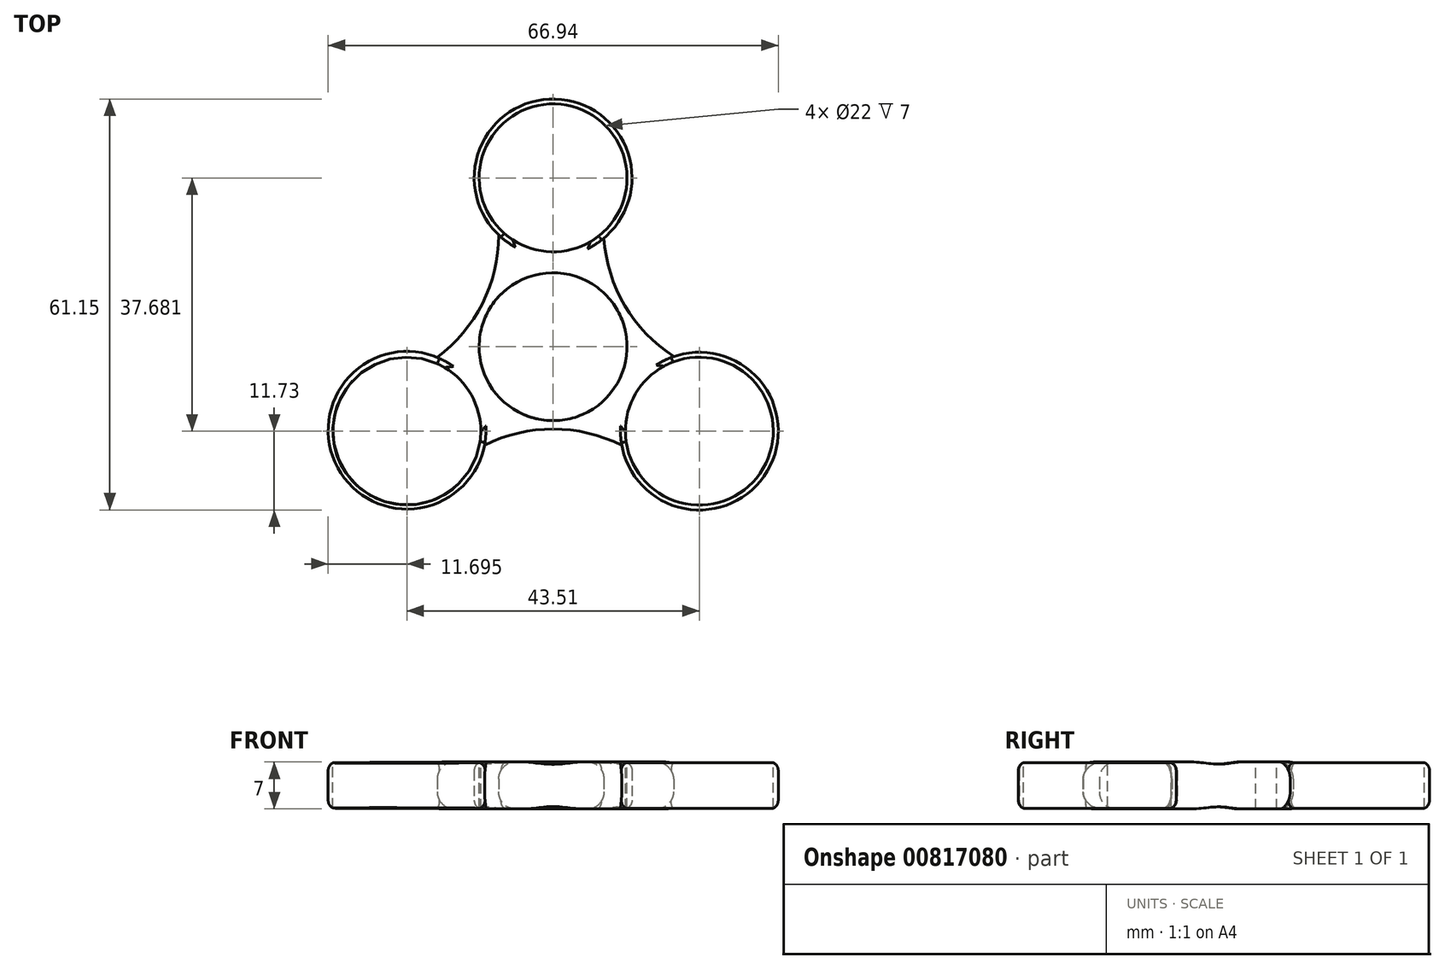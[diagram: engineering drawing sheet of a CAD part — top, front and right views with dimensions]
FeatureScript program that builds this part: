
annotation { "Feature Type Name" : "Feature", "Feature Type Description" : "" }
export const myFeature = defineFeature(function(context is Context, id is Id, definition is map)
    precondition{}
    {
        {
            var Q0;
            Q0=qCreatedBy(makeId("Top.planeOp"),FACE);
            var sketch = newSketch(context, id + "F0", { "sketchPlane" : qUnion([Q0])});
            skLineSegment(sketch, "E0.bottom", {"start": v(6.33, 35) * mm, "end": v(4.84, 35) * mm});
            skPoint(sketch, "E0.middle", {"position": v(0, 0) * mm});
            skCircle(sketch, "E1", {"center": v(0, 0) * mm, "radius": 11 * mm});
            skLineSegment(sketch, "E2", {"start": v(0, 0) * mm, "end": v(0, 35) * mm});
            skLineSegment(sketch, "E3", {"start": v(0, 0) * mm, "end": v(31.92, -18.43) * mm});
            skLineSegment(sketch, "E4.MirrorCS", {"start": v(0, 0) * mm, "end": v(-35, -20.2) * mm});
            skCircle(sketch, "E5", {"center": v(-21.75, -12.56) * mm, "radius": 11 * mm});
            skCircle(sketch, "E6", {"center": v(0, 25.12) * mm, "radius": 11 * mm});
            skCircle(sketch, "E7", {"center": v(21.75, -12.56) * mm, "radius": 11 * mm});
            skCircle(sketch, "E8", {"center": v(21.75, -12.56) * mm, "radius": 11.73 * mm});
            skCircle(sketch, "E9", {"center": v(-21.72, -12.43) * mm, "radius": 11.73 * mm});
            skCircle(sketch, "E10", {"center": v(0, 0) * mm, "radius": 11.73 * mm});
            skCircle(sketch, "E11", {"center": v(0, 25.12) * mm, "radius": 11.73 * mm});
            skArc(sketch, "E12", {"start": v(10.21, -14.67) * mm, "mid": v(0, -12.25) * mm, "end": v(-10.2, -14.66) * mm});
            skArc(sketch, "E13", {"start": v(-17.24, -1.59) * mm, "mid": v(-10.5, 6.43) * mm, "end": v(-8.08, 16.61) * mm});
            skArc(sketch, "E14", {"start": v(7.56, 16.15) * mm, "mid": v(10.67, 6.11) * mm, "end": v(17.96, -1.46) * mm});
            skPoint(sketch, "E15.orphan", {"position": v(-35, 35) * mm});
            skLineSegment(sketch, "E16.trimOffspring", {"start": v(-4.84, 35) * mm, "end": v(-6.33, 35) * mm});
            skPoint(sketch, "E17.orphan", {"position": v(35, 35) * mm});
            skPoint(sketch, "E0.right.end.orphan", {"position": v(-35, -35) * mm});
            skPoint(sketch, "E0.left.end.orphan", {"position": v(35, -35) * mm});
            skPoint(sketch, "E18.orphan", {"position": v(35, -20.2) * mm});
            skSolve(sketch);
        }
        {
            var Q0;
            {var subQ0=sQuery(id+"F0.wireOp",EDGE,"E8");var subQ2=sQuery(id+"F0.wireOp",EDGE,"E3");var subQ3=makeQuery(id+"F0.imprint","INTERSECT",VERTEX,{"disambiguationData":[OD(1.0)],"derivedFrom":[subQ2,subQ0]});Q0=makeQuery(id+"F0.imprint","IMPRINT",FACE,{"disambiguationData":[TD([[makeQuery(id+"F0.imprint","IMPRINT",EDGE,{"disambiguationData":[TD([[subQ3,-1.0]])],"derivedFrom":subQ2}),1.0]])]});}
            var Q1;
            {var subQ5=sQuery(id+"F0.wireOp",EDGE,"E14");Q1=makeQuery(id+"F0.imprint","IMPRINT",FACE,{"disambiguationData":[TD([[makeQuery(id+"F0.imprint","IMPRINT",EDGE,{"derivedFrom":subQ5}),-1.0]])]});}
            var Q2;
            {var subQ5=sQuery(id+"F0.wireOp",EDGE,"E0.bottom");Q2=makeQuery(id+"F0.imprint","IMPRINT",FACE,{"disambiguationData":[TD([[makeQuery(id+"F0.imprint","IMPRINT",EDGE,{"derivedFrom":subQ5}),1.0]])]});}
            var Q3;
            {var subQ6=sQuery(id+"F0.wireOp",EDGE,"E16.trimOffspring");Q3=makeQuery(id+"F0.imprint","IMPRINT",FACE,{"disambiguationData":[TD([[makeQuery(id+"F0.imprint","IMPRINT",EDGE,{"derivedFrom":subQ6}),1.0]])]});}
            var Q4;
            {var subQ0=sQuery(id+"F0.wireOp",EDGE,"E2");var subQ1=sQuery(id+"F0.wireOp",EDGE,"E1");var subQ2=makeQuery(id+"F0.imprint","INTERSECT",VERTEX,{"derivedFrom":[subQ1,subQ0]});Q4=makeQuery(id+"F0.imprint","IMPRINT",FACE,{"disambiguationData":[TD([[makeQuery(id+"F0.imprint","IMPRINT",EDGE,{"disambiguationData":[TD([[subQ2,1.0]])],"derivedFrom":subQ1}),-1.0]])]});}
            var Q5;
            {var subQ0=sQuery(id+"F0.wireOp",EDGE,"E4.MirrorCS");var subQ1=sQuery(id+"F0.wireOp",EDGE,"E1");var subQ2=makeQuery(id+"F0.imprint","INTERSECT",VERTEX,{"derivedFrom":[subQ1,subQ0]});Q5=makeQuery(id+"F0.imprint","IMPRINT",FACE,{"disambiguationData":[TD([[makeQuery(id+"F0.imprint","IMPRINT",EDGE,{"disambiguationData":[TD([[subQ2,1.0]])],"derivedFrom":subQ1}),-1.0]])]});}
            var Q6;
            {var subQ0=sQuery(id+"F0.wireOp",EDGE,"E4.MirrorCS");var subQ1=sQuery(id+"F0.wireOp",EDGE,"E1");var subQ2=makeQuery(id+"F0.imprint","INTERSECT",VERTEX,{"derivedFrom":[subQ1,subQ0]});Q6=makeQuery(id+"F0.imprint","IMPRINT",FACE,{"disambiguationData":[TD([[makeQuery(id+"F0.imprint","IMPRINT",EDGE,{"disambiguationData":[TD([[subQ2,-1.0]])],"derivedFrom":subQ1}),-1.0]])]});}
            var Q7;
            {var subQ0=sQuery(id+"F0.wireOp",EDGE,"E0.bottom");Q7=makeQuery(id+"F0.imprint","IMPRINT",FACE,{"disambiguationData":[TD([[makeQuery(id+"F0.imprint","IMPRINT",EDGE,{"derivedFrom":subQ0}),-1.0]])]});}
            var Q8;
            {var subQ0=sQuery(id+"F0.wireOp",EDGE,"E5");var subQ1=sQuery(id+"F0.wireOp",EDGE,"E4.MirrorCS");var subQ2=makeQuery(id+"F0.imprint","INTERSECT",VERTEX,{"disambiguationData":[OD(0.0)],"derivedFrom":[subQ1,subQ0]});Q8=makeQuery(id+"F0.imprint","IMPRINT",FACE,{"disambiguationData":[TD([[makeQuery(id+"F0.imprint","IMPRINT",EDGE,{"disambiguationData":[TD([[subQ2,-1.0]])],"derivedFrom":subQ1}),1.0]])]});}
            var Q9;
            {var subQ0=sQuery(id+"F0.wireOp",EDGE,"E7");var subQ1=sQuery(id+"F0.wireOp",EDGE,"E3");var subQ2=makeQuery(id+"F0.imprint","INTERSECT",VERTEX,{"disambiguationData":[OD(0.0)],"derivedFrom":[subQ1,subQ0]});Q9=makeQuery(id+"F0.imprint","IMPRINT",FACE,{"disambiguationData":[TD([[makeQuery(id+"F0.imprint","IMPRINT",EDGE,{"disambiguationData":[TD([[subQ2,-1.0]])],"derivedFrom":subQ1}),-1.0]])]});}
            var Q10;
            {var subQ0=sQuery(id+"F0.wireOp",EDGE,"E2");var subQ1=sQuery(id+"F0.wireOp",EDGE,"E1");var subQ2=makeQuery(id+"F0.imprint","INTERSECT",VERTEX,{"derivedFrom":[subQ1,subQ0]});Q10=makeQuery(id+"F0.imprint","IMPRINT",FACE,{"disambiguationData":[TD([[makeQuery(id+"F0.imprint","IMPRINT",EDGE,{"disambiguationData":[TD([[subQ2,1.0]])],"derivedFrom":subQ1}),1.0]])]});}
            var Q11;
            {var subQ0=sQuery(id+"F0.wireOp",EDGE,"E4.MirrorCS");var subQ1=sQuery(id+"F0.wireOp",EDGE,"E1");var subQ2=makeQuery(id+"F0.imprint","INTERSECT",VERTEX,{"derivedFrom":[subQ1,subQ0]});Q11=makeQuery(id+"F0.imprint","IMPRINT",FACE,{"disambiguationData":[TD([[makeQuery(id+"F0.imprint","IMPRINT",EDGE,{"disambiguationData":[TD([[subQ2,-1.0]])],"derivedFrom":subQ1}),1.0]])]});}
            var Q12;
            {var subQ0=sQuery(id+"F0.wireOp",EDGE,"E5");var subQ1=sQuery(id+"F0.wireOp",EDGE,"E4.MirrorCS");var subQ2=makeQuery(id+"F0.imprint","INTERSECT",VERTEX,{"disambiguationData":[OD(0.0)],"derivedFrom":[subQ1,subQ0]});Q12=makeQuery(id+"F0.imprint","IMPRINT",FACE,{"disambiguationData":[TD([[makeQuery(id+"F0.imprint","IMPRINT",EDGE,{"disambiguationData":[TD([[subQ2,-1.0]])],"derivedFrom":subQ1}),-1.0]])]});}
            var Q13;
            {var subQ0=sQuery(id+"F0.wireOp",EDGE,"E12");Q13=makeQuery(id+"F0.imprint","IMPRINT",FACE,{"disambiguationData":[TD([[makeQuery(id+"F0.imprint","IMPRINT",EDGE,{"derivedFrom":subQ0}),-1.0]])]});}
            var Q14;
            {var subQ0=sQuery(id+"F0.wireOp",EDGE,"E7");var subQ1=sQuery(id+"F0.wireOp",EDGE,"E3");var subQ2=makeQuery(id+"F0.imprint","INTERSECT",VERTEX,{"disambiguationData":[OD(0.0)],"derivedFrom":[subQ1,subQ0]});Q14=makeQuery(id+"F0.imprint","IMPRINT",FACE,{"disambiguationData":[TD([[makeQuery(id+"F0.imprint","IMPRINT",EDGE,{"disambiguationData":[TD([[subQ2,-1.0]])],"derivedFrom":subQ1}),1.0]])]});}
            var Q15;
            {var subQ0=sQuery(id+"F0.wireOp",EDGE,"E9");var subQ2=sQuery(id+"F0.wireOp",EDGE,"E4.MirrorCS");var subQ3=makeQuery(id+"F0.imprint","INTERSECT",VERTEX,{"disambiguationData":[OD(1.0)],"derivedFrom":[subQ2,subQ0]});Q15=makeQuery(id+"F0.imprint","IMPRINT",FACE,{"disambiguationData":[TD([[makeQuery(id+"F0.imprint","IMPRINT",EDGE,{"disambiguationData":[TD([[subQ3,-1.0]])],"derivedFrom":subQ2}),-1.0]])]});}
            var Q16;
            {var subQ5=sQuery(id+"F0.wireOp",EDGE,"E13");Q16=makeQuery(id+"F0.imprint","IMPRINT",FACE,{"disambiguationData":[TD([[makeQuery(id+"F0.imprint","IMPRINT",EDGE,{"derivedFrom":subQ5}),-1.0]])]});}
            var Q17;
            {var subQ0=sQuery(id+"F0.wireOp",EDGE,"E9");var subQ2=sQuery(id+"F0.wireOp",EDGE,"E4.MirrorCS");var subQ7=makeQuery(id+"F0.imprint","INTERSECT",VERTEX,{"disambiguationData":[OD(1.0)],"derivedFrom":[subQ2,subQ0]});Q17=makeQuery(id+"F0.imprint","IMPRINT",FACE,{"disambiguationData":[TD([[makeQuery(id+"F0.imprint","IMPRINT",EDGE,{"disambiguationData":[TD([[subQ7,-1.0]])],"derivedFrom":subQ2}),1.0]])]});}
            var Q18;
            {var subQ0=sQuery(id+"F0.wireOp",EDGE,"E6");var subQ1=makeQuery(id+"F0.imprint","INTERSECT",VERTEX,{"derivedFrom":[sQuery(id+"F0.wireOp",EDGE,"E0.bottom"),subQ0]});Q18=makeQuery(id+"F0.imprint","IMPRINT",FACE,{"disambiguationData":[TD([[makeQuery(id+"F0.imprint","IMPRINT",EDGE,{"disambiguationData":[TD([[subQ1,-1.0]])],"derivedFrom":subQ0}),1.0]])]});}
            var Q19;
            {var subQ1=sQuery(id+"F0.wireOp",EDGE,"E3");var subQ4=sQuery(id+"F0.wireOp",EDGE,"E8");var subQ6=makeQuery(id+"F0.imprint","INTERSECT",VERTEX,{"disambiguationData":[OD(1.0)],"derivedFrom":[subQ1,subQ4]});Q19=makeQuery(id+"F0.imprint","IMPRINT",FACE,{"disambiguationData":[TD([[makeQuery(id+"F0.imprint","IMPRINT",EDGE,{"disambiguationData":[TD([[subQ6,-1.0]])],"derivedFrom":subQ1}),-1.0]])]});}
            var Q20;
            {var subQ0=sQuery(id+"F0.wireOp",EDGE,"E4.MirrorCS");var subQ1=sQuery(id+"F0.wireOp",EDGE,"E1");var subQ2=makeQuery(id+"F0.imprint","INTERSECT",VERTEX,{"derivedFrom":[subQ1,subQ0]});Q20=makeQuery(id+"F0.imprint","IMPRINT",FACE,{"disambiguationData":[TD([[makeQuery(id+"F0.imprint","IMPRINT",EDGE,{"disambiguationData":[TD([[subQ2,1.0]])],"derivedFrom":subQ1}),1.0]])]});}
            extrude(context, id + "F1", {"entities" : qUnion([Q0, Q1, Q2, Q3, Q4, Q5, Q6, Q7, Q8, Q9, Q10, Q11, Q12, Q13, Q14, Q15, Q16, Q17, Q18, Q19, Q20]), "depth" : 7 * mm, "offsetDistance" : 25.4 * mm});
        }
        {
            var Q0;
            Q0=sQuery(id+"F0.wireOp",VERTEX,"E6.center");
            var Q1;
            Q1=sQuery(id+"F0.wireOp",VERTEX,"E0.middle");
            var Q2;
            Q2=sQuery(id+"F0.wireOp",VERTEX,"E7.center");
            var Q3;
            Q3=sQuery(id+"F0.wireOp",VERTEX,"E5.center");
            var Q4;
            Q4=makeQuery(id+"F1.opExtrude","SWEPT_BODY",BODY,{"disambiguationData":[OSD([sQuery(id+"F0.wireOp",EDGE,"E8"),sQuery(id+"F0.wireOp",EDGE,"E9"),sQuery(id+"F0.wireOp",EDGE,"E11"),sQuery(id+"F0.wireOp",EDGE,"E12"),sQuery(id+"F0.wireOp",EDGE,"E13"),sQuery(id+"F0.wireOp",EDGE,"E14")])]});
            hole(context, id + "F2", {"style" : HoleStyle.SIMPLE, "endStyle" : HoleEndStyle.THROUGH, "oppositeDirection" : true, "holeDiameter" : 22 * mm, "majorDiameter" : 6.35 * mm, "isTappedThrough" : true, "tappedDepth" : 12.7 * mm, "tapClearance" : 3, "locations" : qUnion([Q0, Q1, Q2, Q3]), "scope" : qUnion([Q4])});
        }
        {
            var Q0;
            Q0=makeQuery(id+"F1.opExtrude","CAP_EDGE",EDGE,{"disambiguationData":[OSD([sQuery(id+"F0.wireOp",EDGE,"E12")])],"isStart":false});
            var Q1;
            Q1=makeQuery(id+"F1.opExtrude","CAP_EDGE",EDGE,{"disambiguationData":[OSD([sQuery(id+"F0.wireOp",EDGE,"E12")])],"isStart":true});
            var Q2;
            Q2=makeQuery(id+"F1.opExtrude","CAP_EDGE",EDGE,{"disambiguationData":[OSD([sQuery(id+"F0.wireOp",EDGE,"E13")])],"isStart":false});
            var Q3;
            Q3=makeQuery(id+"F1.opExtrude","CAP_EDGE",EDGE,{"disambiguationData":[OSD([sQuery(id+"F0.wireOp",EDGE,"E14")])],"isStart":false});
            var Q4;
            Q4=makeQuery(id+"F1.opExtrude","CAP_EDGE",EDGE,{"disambiguationData":[OSD([sQuery(id+"F0.wireOp",EDGE,"E14")])],"isStart":true});
            var Q5;
            Q5=makeQuery(id+"F1.opExtrude","CAP_EDGE",EDGE,{"disambiguationData":[OSD([sQuery(id+"F0.wireOp",EDGE,"E13")])],"isStart":true});
            fillet(context, id + "F3", {"entities" : qUnion([Q0, Q1, Q2, Q3, Q4, Q5]), "radius" : 2.54 * mm, "tangentPropagation" : true, "allowEdgeOverflow" : false});
        }
        {
            var Q0;
            Q0=makeQuery(id+"F1.opExtrude","CAP_EDGE",EDGE,{"disambiguationData":[OSD([sQuery(id+"F0.wireOp",EDGE,"E11")])],"isStart":true});
            var Q1;
            Q1=makeQuery(id+"F1.opExtrude","CAP_EDGE",EDGE,{"disambiguationData":[OSD([sQuery(id+"F0.wireOp",EDGE,"E11")])],"isStart":false});
            var Q2;
            Q2=makeQuery(id+"F1.opExtrude","CAP_EDGE",EDGE,{"disambiguationData":[OSD([sQuery(id+"F0.wireOp",EDGE,"E8")])],"isStart":false});
            var Q3;
            Q3=makeQuery(id+"F1.opExtrude","CAP_EDGE",EDGE,{"disambiguationData":[OSD([sQuery(id+"F0.wireOp",EDGE,"E8")])],"isStart":true});
            var Q4;
            Q4=makeQuery(id+"F1.opExtrude","CAP_EDGE",EDGE,{"disambiguationData":[OSD([sQuery(id+"F0.wireOp",EDGE,"E9")])],"isStart":false});
            var Q5;
            Q5=makeQuery(id+"F1.opExtrude","CAP_EDGE",EDGE,{"disambiguationData":[OSD([sQuery(id+"F0.wireOp",EDGE,"E9")])],"isStart":true});
            fillet(context, id + "F4", {"entities" : qUnion([Q0, Q1, Q2, Q3, Q4, Q5]), "radius" : 1.27 * mm, "tangentPropagation" : true, "allowEdgeOverflow" : false});
        }
    });
